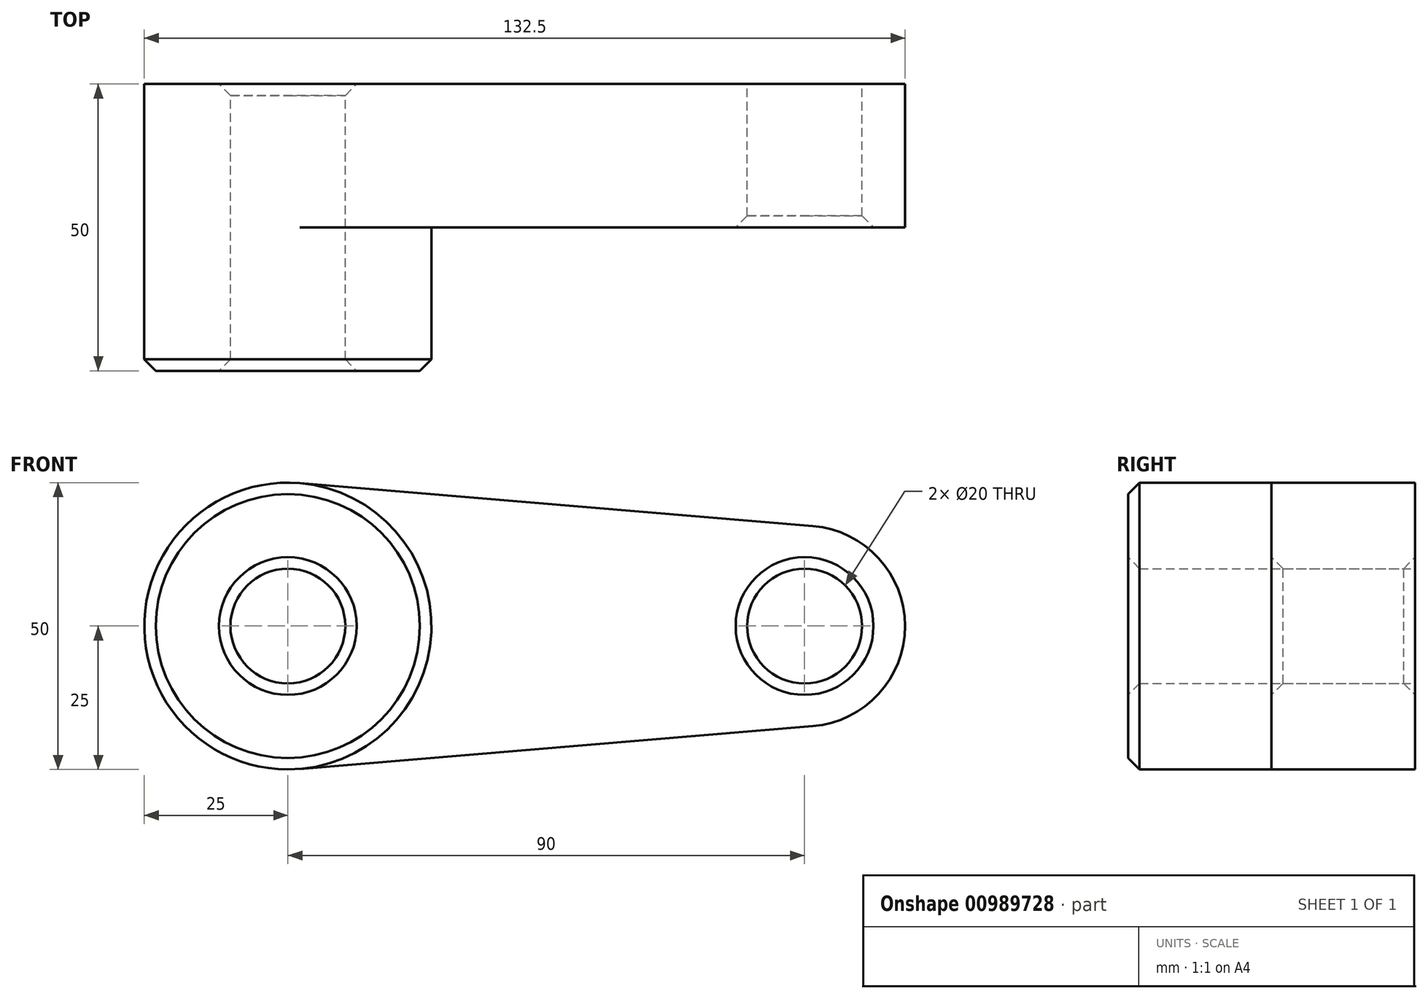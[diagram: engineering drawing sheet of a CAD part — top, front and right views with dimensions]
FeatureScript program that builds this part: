
annotation { "Feature Type Name" : "Feature", "Feature Type Description" : "" }
export const myFeature = defineFeature(function(context is Context, id is Id, definition is map)
    precondition{}
    {
        {
            var Q0;
            Q0=qCreatedBy(makeId("Front.planeOp"),FACE);
            var sketch = newSketch(context, id + "F0", { "sketchPlane" : qUnion([Q0])});
            skCircle(sketch, "E0", {"center": v(0, 0) * mm, "radius": 25 * mm});
            skCircle(sketch, "E1", {"center": v(90, 0) * mm, "radius": 17.5 * mm});
            skLineSegment(sketch, "E2", {"start": v(2.08, -24.91) * mm, "end": v(91.46, -17.44) * mm});
            skLineSegment(sketch, "E3", {"start": v(2.08, 24.91) * mm, "end": v(91.46, 17.44) * mm});
            skCircle(sketch, "E4", {"center": v(0, 0) * mm, "radius": 10 * mm});
            skCircle(sketch, "E5", {"center": v(90, 0) * mm, "radius": 10 * mm});
            skSolve(sketch);
        }
        {
            var Q0;
            Q0 = qSketchRegion(id + "F0", true);
            extrude(context, id + "F1", {"entities" : qUnion([Q0]), "depth" : 25 * mm, "offsetDistance" : 25 * mm});
        }
        {
            var Q0;
            Q0=makeQuery(id+"F0.imprint","IMPRINT",FACE,{"disambiguationData":[TD([[makeQuery(id+"F0.imprint","IMPRINT",EDGE,{"derivedFrom":sQuery(id+"F0.wireOp",EDGE,"E4")}),-1.0]])]});
            extrude(context, id + "F2", {"entities" : qUnion([Q0]), "operationType" : NewBodyOperationType.ADD, "depth" : 50 * mm, "offsetDistance" : 25 * mm});
        }
        {
            var Q0;
            Q0=makeQuery(id+"F2.opExtrude","CAP_FACE",FACE,{"disambiguationData":[OSD([sQuery(id+"F0.wireOp",EDGE,"E0"),sQuery(id+"F0.wireOp",EDGE,"E4")])],"isStart":false});
            var Q1;
            {var subQ0=sQuery(id+"F0.wireOp",EDGE,"E4");Q1=makeQuery(id+"F2.boolean.opBoolean","MERGE",FACE,{"derivedFrom":[makeQuery(id+"F1.opExtrude","SWEPT_FACE",FACE,{"disambiguationData":[OSD([subQ0])]}),makeQuery(id+"F2.opExtrude","SWEPT_FACE",FACE,{"disambiguationData":[OSD([subQ0])]})]});}
            var Q2;
            Q2=makeQuery(id+"F1.opExtrude","CAP_EDGE",EDGE,{"disambiguationData":[OSD([sQuery(id+"F0.wireOp",EDGE,"E5")])],"isStart":false});
            chamfer(context, id + "F3", {"entities" : qUnion([Q0, Q1, Q2]), "width" : 2 * mm, "tangentPropagation" : true});
        }
    });
